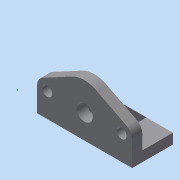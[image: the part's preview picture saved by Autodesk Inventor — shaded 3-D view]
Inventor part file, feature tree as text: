
AUTODESK INVENTOR PART (.ipt)
format: ipt  version: 2015 (Build 190159000, 159)  size: 358,912 bytes
history: native  units: in
note: dims shown in document units (in); Inventor stores cm internally (conversion verified against a paired STEP export)
features: sketch x17, extrude x13, hole x3, projected_geometry x2, mirror x1, fillet x1, chamfer x1, other x1
ambient origin geometry x8: Origin, YZ Plane, XZ Plane, XY Plane, X Axis, Y Axis, Z Axis, Center Point
bodies: Solid1 (feature_tree)
feature tree (39):
  extrude  "Extrusion1"  Depth=1.9685in
  sketch  "Sketch2"  dims[d2=0.7874in d3=0.0in d4=0.1969in]
  extrude  "Extrusion2"  Depth=0.1969in
  extrude  "Extrusion3"  Depth=0.1969in TaperAngle=0.0deg
  extrude  "Extrusion5"  Depth=0.1969in
  hole  "Hole1"  [1 undecoded]
  hole  "Hole2"  [1 undecoded]
  hole  "Hole3"  [1 undecoded]
  extrude  "Extrusion6"  Depth=0.5906in
  extrude  "Extrusion7"  Depth=0.5906in
  mirror  "Mirror1"
  sketch  "Sketch9"  dims[d30=0.5906in d31=0.4724in]
  fillet  "Fillet1"  Radius=0.3937in
  extrude  "Extrusion8"  Depth=0.3937in
  sketch  "Sketch11"  dims[d41=0.3937in d42=0.4724in]
  extrude  "Extrusion9"  Depth=0.1969in TaperAngle=0.0deg
  extrude  "Extrusion10"  TaperAngle=0.0deg  [1 undecoded]
  extrude  "Extrusion11"  Depth=0.344in
  chamfer  "Chamfer1"  Distance=0.333in
  extrude  "Extrusion12"  TaperAngle=0.0deg  [1 undecoded]
  extrude  "Extrusion13"  Depth=0.5906in TaperAngle=0.0deg
  extrude  "Extrusion14"  Depth=0.5906in TaperAngle=0.0deg
  sketch  "Sketch1"  dims[d0=1.9685in d1=1.9685in]
  sketch  "Sketch3"  dims[d5=0.1969in d6=0.2953in d7=0.0in]
  sketch  "Sketch4"  dims[d8=0.1969in d9=0.0in d12=0.5in]
  sketch  "Sketch5"  dims[d13=0.5in d14=0.0in d15=0.0in]
  sketch  "Sketch6"  dims[d17=0.2756in]
  sketch  "Sketch7"  dims[d20=0.315in d21=0.75in d22=0.375in d23=0.25in d24=0.5635in d25=1.0in d26=0.8108in d27=0.2756in]
  sketch  "Sketch8"  dims[d28=0.3937in d29=0.3937in]
  sketch  "Sketch10"  dims[d32=0.1969in d33=0.75in d34=0.375in d35=0.25in d36=0.5635in d37=1.0in d38=0.8108in d39=0.5906in d40=0.3937in]
  other  "Image1"
  sketch  "Sketch12"  dims[d43=0.1969in d44=0.75in d45=0.375in d46=0.25in d47=0.5635in d48=1.0in d49=0.8108in d50=1.0in d51=0.0in]
  sketch  "Sketch13"  dims[d52=0.0in d53=0.0in d54=0.0in]
  sketch  "Sketch14"  dims[d55=0.315in d56=0.344in]
  sketch  "Sketch15"  dims[d57=0.333in]
  projected_geometry  "Projected Loop1"
  sketch  "Sketch16"  dims[d58=0.5in]
  projected_geometry  "Projected Loop2"
  sketch  "Sketch17"  dims[d59=0.5in d60=0.333in d61=0.0in d62=1.0in d63=0.0in d79=1.0in d80=0.0in d81=1.0in d82=0.0in d83=0.3937in d84=0.1969in d85=0.3937in d86=0.1969in d87=0.5906in d88=0.0in d89=0.5906in d90=0.0787in d91=45.0deg d92=0.1181in d93=0.0in d94=0.1181in d95=0.0in d96=0.0in d97=0.0in]
note: 5 required parameter values undecoded (feature->parameter linkage not recoverable at this tier; creation-order binding heuristic only, values carry confidence <= 0.55)
